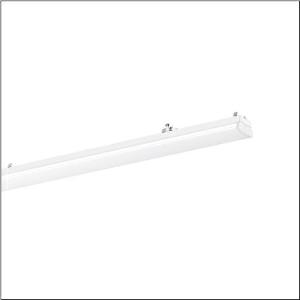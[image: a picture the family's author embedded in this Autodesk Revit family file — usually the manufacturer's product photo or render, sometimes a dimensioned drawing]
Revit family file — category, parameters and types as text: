
# Revit family: licross_r__11_recessed_opal_mo_51tl1ddv4e5g_e7a4
name_source: partatom
category: Lighting Fixtures
units: mm (PartAtom-declared; Revit-internal decimal feet)

## family parameters
Cut with Voids When Loaded = No
Host = Face
Light Source = No
Part Type = Normal
Room Calculation Point = No
Round Connector Dimension = Use Diameter
Shared = No

## types (1)
- --- (1 x LED, 14560 lm, 84.1 W, 4000K)
    Apparent Load = 84 VA
    CIE Flux Codes = 44 73 91 87 100
    Color Rendering = 80
    Color Temperature = 4000K
    Default Elevation = 1800 mm
    Description = Licross® 11 recessed opal MO, luminaire insert, of sheet steel, coil coated, white, length: 2.250mm, width: 76mm, height: 87mm, LED rated luminous flux: 14.560lm, light colour: 840, control gear: DALI 2, with plug, 5-pole, with phase selection, mains connection: 220..240V, AC, 50/60Hz, rated input power: 84W, halogen-free wiring, primary optical cover: cover, of PMMA, light emission: direct with ceiling illumination distribution, primary light characteristic: symmetric, protection rating (complete): IP40, insulation class (complete): insulation class I (protective earthing), certification: CE, ENEC, VDE, UKCA, protection symbol: D if used in an environment without relevant dust loads with corresponding accessories, impact resistance: IK06, permissible ambient temperature for indoor applications: -25..+35°C, corresponds to IFS (International Featured Standards) requirements for safety and quality in the food industry, reducing of maximum allowable ambient temperature of 5°C with ceiling mounting, LABS conformity tested according to VDMA 24364:2018-05, packaging unit: 1 piece
    Height = 83 mm
    Lamp = 1 x LED
    Lamp Light Flux = 14560 lm
    Lamp Power = 84.1 W
    Lamp count = 1
    Length = 2250 mm
    Luminous efficacy = 173 lm/W
    Manufacturer = Siteco
    ModVariant = No
    Model = 51TL1DDV4E5G
    Mounting Place = Ceiling
    Mounting Type = Pendant
    Number of Poles = 1
    OnlyDefault = Yes
    Power Factor = 1
    Product Name = Licross® 11 recessed opal MO
    Product group = luminaire insert
    ProductGroupID = 901
    Protection Class = Protection class I
    Protection Degree = IP 40
    RLX_Detail_Level = 1
    RLX_Emergency_Light_Flux = 0 lm
    RLX_Emergency_Type = 0
    RLX_Emergency_Type_DB = No
    RlxData = <blob elided: 18189 chars, md5=2253945e>
    Socket = socket
    Standby Power = 0 W
    System Light Flux = 14560 lm
    System Power = 84 W
    Type Comments = factory setting: luminous flux: 100 % | dim-lin: 254 | 378 mA
    Type Image = l_1313666.jpg
    URL = http://relux.com
    VarID = @adj_027587
    Voltage = 0 V
    Weight = 0.00 kg
    Width = 76 mm

## geometry (parser evidence)
native form markers: Blend x4, Sweep x11
no freeform markers — native parametric forms only
